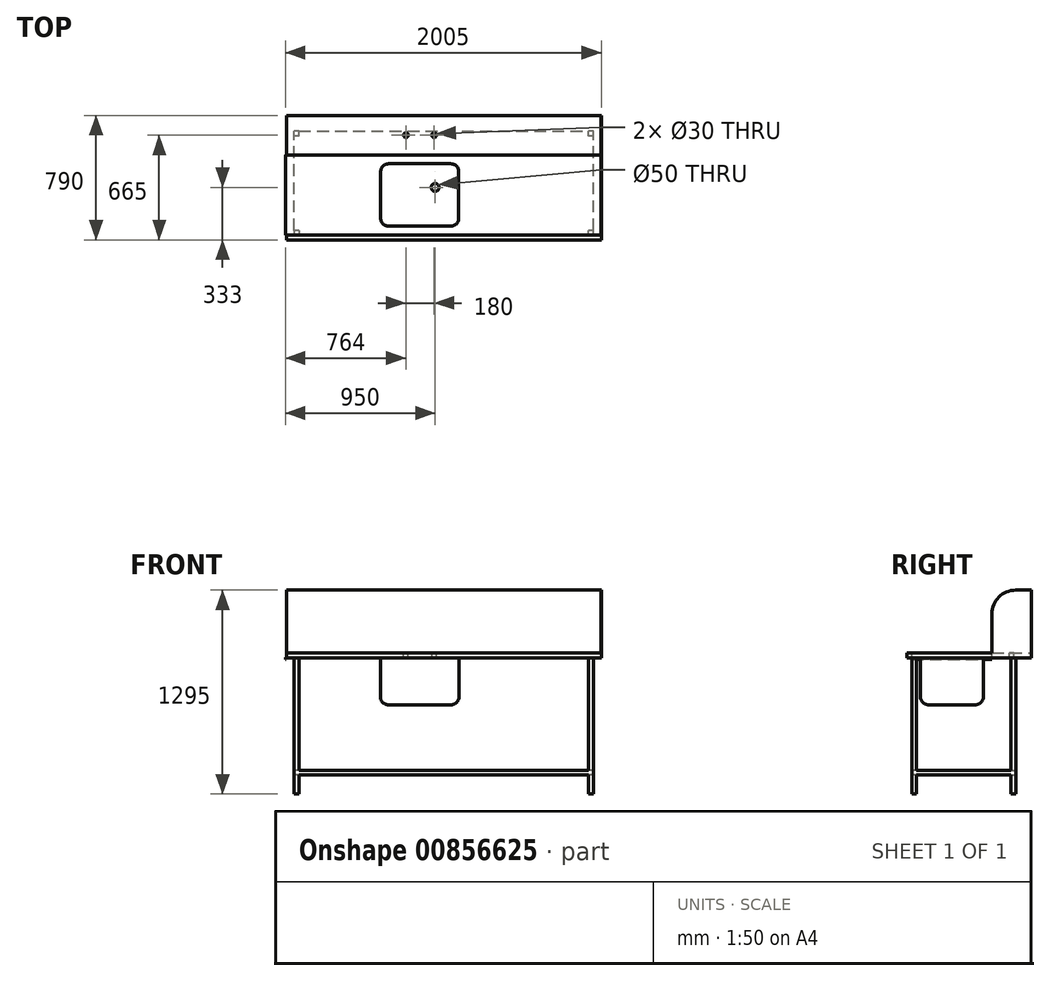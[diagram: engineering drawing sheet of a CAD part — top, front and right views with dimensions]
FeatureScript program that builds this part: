
annotation { "Feature Type Name" : "Feature", "Feature Type Description" : "" }
export const myFeature = defineFeature(function(context is Context, id is Id, definition is map)
    precondition{}
    {
        {
            var Q0;
            Q0=qCreatedBy(makeId("Top.planeOp"),FACE);
            var sketch = newSketch(context, id + "F0", { "sketchPlane" : qUnion([Q0])});
            skLineSegment(sketch, "E0.bottom", {"start": v(0, 0) * mm, "end": v(2000, 0) * mm});
            skLineSegment(sketch, "E0.top", {"start": v(0, 790) * mm, "end": v(2000, 790) * mm});
            skLineSegment(sketch, "E0.left", {"start": v(0, 0) * mm, "end": v(0, 790) * mm});
            skLineSegment(sketch, "E0.right", {"start": v(2000, 0) * mm, "end": v(2000, 790) * mm});
            skSolve(sketch);
        }
        {
            var Q0;
            Q0 = qSketchRegion(id + "F0", true);
            extrude(context, id + "F1", {"entities" : qUnion([Q0]), "depth" : 30 * mm, "offsetDistance" : 25 * mm});
        }
        {
            var Q0;
            Q0=makeQuery(id+"F1.opExtrude","CAP_FACE",FACE,{"disambiguationData":[OSD([sQuery(id+"F0.wireOp",EDGE,"E0.bottom"),sQuery(id+"F0.wireOp",EDGE,"E0.top"),sQuery(id+"F0.wireOp",EDGE,"E0.left"),sQuery(id+"F0.wireOp",EDGE,"E0.right")])],"isStart":false});
            var sketch = newSketch(context, id + "F2", { "sketchPlane" : qUnion([Q0])});
            skLineSegment(sketch, "E1.bottom", {"start": v(0, 30) * mm, "end": v(1998, 30) * mm});
            skLineSegment(sketch, "E1.top", {"start": v(0, 540) * mm, "end": v(1998, 540) * mm});
            skLineSegment(sketch, "E1.left", {"start": v(0, 30) * mm, "end": v(0, 540) * mm});
            skLineSegment(sketch, "E1.right", {"start": v(1998, 30) * mm, "end": v(1998, 540) * mm});
            skSolve(sketch);
        }
        {
            var Q0;
            Q0 = qSketchRegion(id + "F2", true);
            extrude(context, id + "F3", {"entities" : qUnion([Q0]), "operationType" : NewBodyOperationType.REMOVE, "oppositeDirection" : true, "depth" : 28 * mm, "offsetDistance" : 25 * mm});
        }
        {
            var Q0;
            Q0=makeQuery(id+"F1.opExtrude","SWEPT_FACE",FACE,{"disambiguationData":[OSD([sQuery(id+"F0.wireOp",EDGE,"E0.left")])]});
            var sketch = newSketch(context, id + "F4", { "sketchPlane" : qUnion([Q0])});
            skLineSegment(sketch, "E2.bottom", {"start": v(-540, 2) * mm, "end": v(-30, 2) * mm});
            skLineSegment(sketch, "E2.top", {"start": v(-540, 0) * mm, "end": v(-30, 0) * mm});
            skLineSegment(sketch, "E2.left", {"start": v(-540, 2) * mm, "end": v(-540, 0) * mm});
            skLineSegment(sketch, "E2.right", {"start": v(-30, 2) * mm, "end": v(-30, 0) * mm});
            skSolve(sketch);
        }
        {
            var Q0;
            Q0 = qSketchRegion(id + "F4", true);
            extrude(context, id + "F5", {"entities" : qUnion([Q0]), "operationType" : NewBodyOperationType.ADD, "depth" : 3 * mm, "offsetDistance" : 25 * mm});
        }
        {
            var Q0;
            Q0=makeQuery(id+"F5.opExtrude","CAP_FACE",FACE,{"disambiguationData":[OSD([sQuery(id+"F4.wireOp",EDGE,"E2.bottom"),sQuery(id+"F4.wireOp",EDGE,"E2.top"),sQuery(id+"F4.wireOp",EDGE,"E2.left"),sQuery(id+"F4.wireOp",EDGE,"E2.right")])],"isStart":false});
            var Q1;
            Q1=makeQuery(id+"F5.opExtrude","CAP_EDGE",EDGE,{"disambiguationData":[OSD([sQuery(id+"F4.wireOp",EDGE,"E2.top")])],"isStart":false});
            revolve(context, id + "F6", {"operationType" : NewBodyOperationType.ADD, "surfaceOperationType" : NewSurfaceOperationType.NEW, "entities" : qUnion([Q0]), "axis" : qUnion([Q1]), "revolveType" : RevolveType.ONE_DIRECTION, "oppositeDirection" : true, "angle" : 90 * degree});
        }
        {
            var Q0;
            {var subQ0=sQuery(id+"F4.wireOp",EDGE,"E2.top");Q0=makeQuery(id+"F6.boolean.opBoolean","MERGE",FACE,{"derivedFrom":[makeQuery(id+"F5.boolean.opBoolean","MERGE",FACE,{"derivedFrom":[makeQuery(id+"F1.opExtrude","CAP_FACE",FACE,{"disambiguationData":[OSD([sQuery(id+"F0.wireOp",EDGE,"E0.bottom"),sQuery(id+"F0.wireOp",EDGE,"E0.top"),sQuery(id+"F0.wireOp",EDGE,"E0.left"),sQuery(id+"F0.wireOp",EDGE,"E0.right")])],"isStart":true}),makeQuery(id+"F5.opExtrude","SWEPT_FACE",FACE,{"disambiguationData":[OSD([subQ0])]})]}),makeQuery(id+"F6.opRevolve","CAP_FACE",FACE,{"disambiguationData":[OSD([sQuery(id+"F4.wireOp",EDGE,"E2.bottom"),subQ0,sQuery(id+"F4.wireOp",EDGE,"E2.left"),sQuery(id+"F4.wireOp",EDGE,"E2.right")])],"isStart":false})]});}
            var sketch = newSketch(context, id + "F7", { "sketchPlane" : qUnion([Q0])});
            skLineSegment(sketch, "E3.bottom", {"start": v(-5, -540) * mm, "end": v(-3, -540) * mm});
            skLineSegment(sketch, "E3.top", {"start": v(-5, -30) * mm, "end": v(-3, -30) * mm});
            skLineSegment(sketch, "E3.left", {"start": v(-5, -540) * mm, "end": v(-5, -30) * mm});
            skLineSegment(sketch, "E3.right", {"start": v(-3, -540) * mm, "end": v(-3, -30) * mm});
            skSolve(sketch);
        }
        {
            var Q0;
            Q0 = qSketchRegion(id + "F7", true);
            extrude(context, id + "F8", {"entities" : qUnion([Q0]), "operationType" : NewBodyOperationType.ADD, "depth" : 10 * mm, "offsetDistance" : 25 * mm});
        }
        {
            var Q0;
            Q0=makeQuery(id+"F5.boolean.opBoolean","MERGE",FACE,{"derivedFrom":[makeQuery(id+"F3.boolean.opBoolean","COPY",FACE,{"derivedFrom":makeQuery(id+"F3.opExtrude","CAP_FACE",FACE,{"disambiguationData":[OSD([sQuery(id+"F2.wireOp",EDGE,"E1.bottom"),sQuery(id+"F2.wireOp",EDGE,"E1.top"),sQuery(id+"F2.wireOp",EDGE,"E1.left"),sQuery(id+"F2.wireOp",EDGE,"E1.right")])],"isStart":false})}),makeQuery(id+"F5.opExtrude","SWEPT_FACE",FACE,{"disambiguationData":[OSD([sQuery(id+"F4.wireOp",EDGE,"E2.bottom")])]})]});
            var sketch = newSketch(context, id + "F9", { "sketchPlane" : qUnion([Q0])});
            skLineSegment(sketch, "E4.bottom", {"start": v(1097, 485) * mm, "end": v(597, 485) * mm});
            skLineSegment(sketch, "E4.top", {"start": v(1097, 85) * mm, "end": v(597, 85) * mm});
            skLineSegment(sketch, "E4.left", {"start": v(1097, 485) * mm, "end": v(1097, 85) * mm});
            skLineSegment(sketch, "E4.right", {"start": v(597, 485) * mm, "end": v(597, 85) * mm});
            skPoint(sketch, "E4.middle", {"position": v(847, 285) * mm});
            skPoint(sketch, "E4.middle.positionSnap0", {"position": v(1998, 285) * mm});
            skPoint(sketch, "E4.middle.positionSnap1", {"position": v(847, 540) * mm});
            skPoint(sketch, "E4.centerSnap0", {"position": v(1998, 285) * mm});
            skPoint(sketch, "E4.centerSnap1", {"position": v(847, 540) * mm});
            skSolve(sketch);
        }
        {
            var Q0;
            Q0 = qSketchRegion(id + "F9", true);
            extrude(context, id + "F10", {"entities" : qUnion([Q0]), "operationType" : NewBodyOperationType.ADD, "oppositeDirection" : true, "depth" : 300 * mm, "offsetDistance" : 25 * mm});
        }
        {
            var Q0;
            Q0=makeQuery(id+"F5.boolean.opBoolean","MERGE",FACE,{"derivedFrom":[makeQuery(id+"F3.boolean.opBoolean","COPY",FACE,{"derivedFrom":makeQuery(id+"F3.opExtrude","CAP_FACE",FACE,{"disambiguationData":[OSD([sQuery(id+"F2.wireOp",EDGE,"E1.bottom"),sQuery(id+"F2.wireOp",EDGE,"E1.top"),sQuery(id+"F2.wireOp",EDGE,"E1.left"),sQuery(id+"F2.wireOp",EDGE,"E1.right")])],"isStart":false})}),makeQuery(id+"F5.opExtrude","SWEPT_FACE",FACE,{"disambiguationData":[OSD([sQuery(id+"F4.wireOp",EDGE,"E2.bottom")])]})]});
            var sketch = newSketch(context, id + "F11", { "sketchPlane" : qUnion([Q0])});
            skLineSegment(sketch, "E5.bottom", {"start": v(1095, 483) * mm, "end": v(599, 483) * mm});
            skLineSegment(sketch, "E5.top", {"start": v(1095, 87) * mm, "end": v(599, 87) * mm});
            skLineSegment(sketch, "E5.left", {"start": v(1095, 483) * mm, "end": v(1095, 87) * mm});
            skLineSegment(sketch, "E5.right", {"start": v(599, 483) * mm, "end": v(599, 87) * mm});
            skPoint(sketch, "E5.middle", {"position": v(847, 285) * mm});
            skPoint(sketch, "E5.middle.positionSnap0", {"position": v(1998, 285) * mm});
            skPoint(sketch, "E5.middle.positionSnap1", {"position": v(847, 540) * mm});
            skPoint(sketch, "E5.centerSnap0", {"position": v(1998, 285) * mm});
            skPoint(sketch, "E5.centerSnap1", {"position": v(847, 540) * mm});
            skSolve(sketch);
        }
        {
            var Q0;
            Q0 = qSketchRegion(id + "F11", true);
            extrude(context, id + "F12", {"entities" : qUnion([Q0]), "operationType" : NewBodyOperationType.REMOVE, "oppositeDirection" : true, "depth" : 298 * mm, "offsetDistance" : 25 * mm});
        }
        {
            var Q0;
            Q0=makeQuery(id+"F12.boolean.opBoolean","COPY",EDGE,{"derivedFrom":makeQuery(id+"F12.opExtrude","SWEPT_EDGE",EDGE,{"disambiguationData":[OSD([sQuery(id+"F11.wireOp",EDGE,"E5.bottom"),sQuery(id+"F11.wireOp",EDGE,"E5.right")])]})});
            var Q1;
            Q1=makeQuery(id+"F12.boolean.opBoolean","COPY",EDGE,{"derivedFrom":makeQuery(id+"F12.opExtrude","SWEPT_EDGE",EDGE,{"disambiguationData":[OSD([sQuery(id+"F11.wireOp",EDGE,"E5.bottom"),sQuery(id+"F11.wireOp",EDGE,"E5.left")])]})});
            var Q2;
            Q2=makeQuery(id+"F12.boolean.opBoolean","COPY",EDGE,{"derivedFrom":makeQuery(id+"F12.opExtrude","SWEPT_EDGE",EDGE,{"disambiguationData":[OSD([sQuery(id+"F11.wireOp",EDGE,"E5.top"),sQuery(id+"F11.wireOp",EDGE,"E5.left")])]})});
            var Q3;
            Q3=makeQuery(id+"F12.boolean.opBoolean","COPY",EDGE,{"derivedFrom":makeQuery(id+"F12.opExtrude","SWEPT_EDGE",EDGE,{"disambiguationData":[OSD([sQuery(id+"F11.wireOp",EDGE,"E5.top"),sQuery(id+"F11.wireOp",EDGE,"E5.right")])]})});
            var Q4;
            Q4=makeQuery(id+"F12.boolean.opBoolean","COPY",EDGE,{"derivedFrom":makeQuery(id+"F12.opExtrude","CAP_EDGE",EDGE,{"disambiguationData":[OSD([sQuery(id+"F11.wireOp",EDGE,"E5.right")])],"isStart":false})});
            var Q5;
            Q5=makeQuery(id+"F12.boolean.opBoolean","COPY",EDGE,{"derivedFrom":makeQuery(id+"F12.opExtrude","CAP_EDGE",EDGE,{"disambiguationData":[OSD([sQuery(id+"F11.wireOp",EDGE,"E5.top")])],"isStart":false})});
            var Q6;
            Q6=makeQuery(id+"F12.boolean.opBoolean","COPY",EDGE,{"derivedFrom":makeQuery(id+"F12.opExtrude","CAP_EDGE",EDGE,{"disambiguationData":[OSD([sQuery(id+"F11.wireOp",EDGE,"E5.left")])],"isStart":false})});
            var Q7;
            Q7=makeQuery(id+"F12.boolean.opBoolean","COPY",EDGE,{"derivedFrom":makeQuery(id+"F12.opExtrude","CAP_EDGE",EDGE,{"disambiguationData":[OSD([sQuery(id+"F11.wireOp",EDGE,"E5.bottom")])],"isStart":false})});
            var Q8;
            Q8=makeQuery(id+"F10.opExtrude","SWEPT_EDGE",EDGE,{"disambiguationData":[OSD([sQuery(id+"F9.wireOp",EDGE,"E4.top"),sQuery(id+"F9.wireOp",EDGE,"E4.right")])]});
            var Q9;
            Q9=makeQuery(id+"F10.opExtrude","SWEPT_EDGE",EDGE,{"disambiguationData":[OSD([sQuery(id+"F9.wireOp",EDGE,"E4.bottom"),sQuery(id+"F9.wireOp",EDGE,"E4.right")])]});
            var Q10;
            Q10=makeQuery(id+"F10.opExtrude","SWEPT_EDGE",EDGE,{"disambiguationData":[OSD([sQuery(id+"F9.wireOp",EDGE,"E4.top"),sQuery(id+"F9.wireOp",EDGE,"E4.left")])]});
            var Q11;
            Q11=makeQuery(id+"F10.opExtrude","SWEPT_EDGE",EDGE,{"disambiguationData":[OSD([sQuery(id+"F9.wireOp",EDGE,"E4.bottom"),sQuery(id+"F9.wireOp",EDGE,"E4.left")])]});
            var Q12;
            Q12=makeQuery(id+"F10.opExtrude","CAP_EDGE",EDGE,{"disambiguationData":[OSD([sQuery(id+"F9.wireOp",EDGE,"E4.left")])],"isStart":false});
            var Q13;
            Q13=makeQuery(id+"F10.opExtrude","CAP_EDGE",EDGE,{"disambiguationData":[OSD([sQuery(id+"F9.wireOp",EDGE,"E4.top")])],"isStart":false});
            var Q14;
            Q14=makeQuery(id+"F10.opExtrude","CAP_EDGE",EDGE,{"disambiguationData":[OSD([sQuery(id+"F9.wireOp",EDGE,"E4.right")])],"isStart":false});
            var Q15;
            Q15=makeQuery(id+"F10.opExtrude","CAP_EDGE",EDGE,{"disambiguationData":[OSD([sQuery(id+"F9.wireOp",EDGE,"E4.bottom")])],"isStart":false});
            fillet(context, id + "F13", {"entities" : qUnion([Q0, Q1, Q2, Q3, Q4, Q5, Q6, Q7, Q8, Q9, Q10, Q11, Q12, Q13, Q14, Q15]), "radius" : 50 * mm, "tangentPropagation" : true, "allowEdgeOverflow" : false});
        }
        {
            var Q0;
            Q0=makeQuery(id+"F12.boolean.opBoolean","COPY",FACE,{"derivedFrom":makeQuery(id+"F12.opExtrude","CAP_FACE",FACE,{"disambiguationData":[OSD([sQuery(id+"F11.wireOp",EDGE,"E5.bottom"),sQuery(id+"F11.wireOp",EDGE,"E5.top"),sQuery(id+"F11.wireOp",EDGE,"E5.left"),sQuery(id+"F11.wireOp",EDGE,"E5.right")])],"isStart":false})});
            var sketch = newSketch(context, id + "F14", { "sketchPlane" : qUnion([Q0])});
            skCircle(sketch, "E6", {"center": v(945, 333) * mm, "radius": 25 * mm});
            skSolve(sketch);
        }
        {
            var Q0;
            Q0 = qSketchRegion(id + "F14", true);
            extrude(context, id + "F15", {"entities" : qUnion([Q0]), "operationType" : NewBodyOperationType.REMOVE, "endBound" : BoundingType.UP_TO_NEXT, "oppositeDirection" : true, "depth" : 25 * mm, "offsetDistance" : 25 * mm});
        }
        {
            var Q0;
            Q0=makeQuery(id+"F1.opExtrude","CAP_FACE",FACE,{"disambiguationData":[OSD([sQuery(id+"F0.wireOp",EDGE,"E0.bottom"),sQuery(id+"F0.wireOp",EDGE,"E0.top"),sQuery(id+"F0.wireOp",EDGE,"E0.left"),sQuery(id+"F0.wireOp",EDGE,"E0.right")])],"isStart":false});
            var sketch = newSketch(context, id + "F16", { "sketchPlane" : qUnion([Q0])});
            skCircle(sketch, "E7", {"center": v(759, 665) * mm, "radius": 15 * mm});
            skPoint(sketch, "E7.centerSnap0", {"position": v(0, 665) * mm});
            skCircle(sketch, "E8", {"center": v(939, 665) * mm, "radius": 15 * mm});
            skSolve(sketch);
        }
        {
            var Q0;
            Q0 = qSketchRegion(id + "F16", true);
            extrude(context, id + "F17", {"entities" : qUnion([Q0]), "operationType" : NewBodyOperationType.REMOVE, "endBound" : BoundingType.UP_TO_NEXT, "oppositeDirection" : true, "depth" : 25 * mm, "offsetDistance" : 25 * mm});
        }
        {
            var Q0;
            {var subQ0=sQuery(id+"F4.wireOp",EDGE,"E2.top");Q0=makeQuery(id+"F6.boolean.opBoolean","MERGE",FACE,{"derivedFrom":[makeQuery(id+"F5.boolean.opBoolean","MERGE",FACE,{"derivedFrom":[makeQuery(id+"F1.opExtrude","CAP_FACE",FACE,{"disambiguationData":[OSD([sQuery(id+"F0.wireOp",EDGE,"E0.bottom"),sQuery(id+"F0.wireOp",EDGE,"E0.top"),sQuery(id+"F0.wireOp",EDGE,"E0.left"),sQuery(id+"F0.wireOp",EDGE,"E0.right")])],"isStart":true}),makeQuery(id+"F5.opExtrude","SWEPT_FACE",FACE,{"disambiguationData":[OSD([subQ0])]})]}),makeQuery(id+"F6.opRevolve","CAP_FACE",FACE,{"disambiguationData":[OSD([sQuery(id+"F4.wireOp",EDGE,"E2.bottom"),subQ0,sQuery(id+"F4.wireOp",EDGE,"E2.left"),sQuery(id+"F4.wireOp",EDGE,"E2.right")])],"isStart":false})]});}
            var sketch = newSketch(context, id + "F18", { "sketchPlane" : qUnion([Q0])});
            skLineSegment(sketch, "E9.bottom", {"start": v(80, -60) * mm, "end": v(50, -60) * mm});
            skLineSegment(sketch, "E9.top", {"start": v(80, -30) * mm, "end": v(50, -30) * mm});
            skLineSegment(sketch, "E9.left", {"start": v(80, -60) * mm, "end": v(80, -30) * mm});
            skLineSegment(sketch, "E9.right", {"start": v(50, -60) * mm, "end": v(50, -30) * mm});
            skPoint(sketch, "E9.middle", {"position": v(65, -45) * mm});
            skLineSegment(sketch, "E10.bottom", {"start": v(1950, -30) * mm, "end": v(1920, -30) * mm});
            skLineSegment(sketch, "E10.top", {"start": v(1950, -60) * mm, "end": v(1920, -60) * mm});
            skLineSegment(sketch, "E10.left", {"start": v(1950, -30) * mm, "end": v(1950, -60) * mm});
            skLineSegment(sketch, "E10.right", {"start": v(1920, -30) * mm, "end": v(1920, -60) * mm});
            skPoint(sketch, "E10.middle", {"position": v(1935, -45) * mm});
            skLineSegment(sketch, "E11.bottom", {"start": v(1950, -660) * mm, "end": v(1920, -660) * mm});
            skLineSegment(sketch, "E11.top", {"start": v(1950, -690) * mm, "end": v(1920, -690) * mm});
            skLineSegment(sketch, "E11.left", {"start": v(1950, -660) * mm, "end": v(1950, -690) * mm});
            skLineSegment(sketch, "E11.right", {"start": v(1920, -660) * mm, "end": v(1920, -690) * mm});
            skPoint(sketch, "E11.middle", {"position": v(1935, -675) * mm});
            skLineSegment(sketch, "E12.bottom", {"start": v(80, -660) * mm, "end": v(50, -660) * mm});
            skLineSegment(sketch, "E12.top", {"start": v(80, -690) * mm, "end": v(50, -690) * mm});
            skLineSegment(sketch, "E12.left", {"start": v(80, -660) * mm, "end": v(80, -690) * mm});
            skLineSegment(sketch, "E12.right", {"start": v(50, -660) * mm, "end": v(50, -690) * mm});
            skPoint(sketch, "E12.middle", {"position": v(65, -675) * mm});
            skSolve(sketch);
        }
        {
            var Q0;
            Q0 = qSketchRegion(id + "F18", true);
            extrude(context, id + "F19", {"entities" : qUnion([Q0]), "operationType" : NewBodyOperationType.ADD, "depth" : 865 * mm, "offsetDistance" : 25 * mm});
        }
        {
            var Q0;
            Q0=makeQuery(id+"F19.opExtrude","CAP_FACE",FACE,{"disambiguationData":[OSD([sQuery(id+"F18.wireOp",EDGE,"E9.bottom"),sQuery(id+"F18.wireOp",EDGE,"E9.top"),sQuery(id+"F18.wireOp",EDGE,"E9.left"),sQuery(id+"F18.wireOp",EDGE,"E9.right")])],"isStart":false});
            cPlane(context, id + "F20", {"entities" : qUnion([Q0]), "cplaneType" : CPlaneType.OFFSET, "offset" : 150 * mm, "oppositeDirection" : true, "width" : 150 * mm, "height" : 150 * mm});
        }
        {
            var Q0;
            Q0=qCreatedBy(id+"F20.planeOp",FACE);
            var sketch = newSketch(context, id + "F21", { "sketchPlane" : qUnion([Q0])});
            skLineSegment(sketch, "E13.bottom", {"start": v(50, -30) * mm, "end": v(1950, -30) * mm});
            skLineSegment(sketch, "E13.top", {"start": v(50, -690) * mm, "end": v(1950, -690) * mm});
            skLineSegment(sketch, "E13.left", {"start": v(50, -30) * mm, "end": v(50, -690) * mm});
            skLineSegment(sketch, "E13.right", {"start": v(1950, -30) * mm, "end": v(1950, -690) * mm});
            skSolve(sketch);
        }
        {
            var Q0;
            Q0 = qSketchRegion(id + "F21", true);
            extrude(context, id + "F22", {"entities" : qUnion([Q0]), "operationType" : NewBodyOperationType.ADD, "depth" : 30 * mm, "offsetDistance" : 25 * mm});
        }
        {
            var Q0;
            Q0=makeQuery(id+"F1.opExtrude","CAP_FACE",FACE,{"disambiguationData":[OSD([sQuery(id+"F0.wireOp",EDGE,"E0.bottom"),sQuery(id+"F0.wireOp",EDGE,"E0.top"),sQuery(id+"F0.wireOp",EDGE,"E0.left"),sQuery(id+"F0.wireOp",EDGE,"E0.right")])],"isStart":false});
            var sketch = newSketch(context, id + "F23", { "sketchPlane" : qUnion([Q0])});
            skLineSegment(sketch, "E14", {"start": v(0, 540) * mm, "end": v(0, 790) * mm});
            skLineSegment(sketch, "E15", {"start": v(0, 790) * mm, "end": v(2000, 790) * mm});
            skLineSegment(sketch, "E16", {"start": v(2000, 790) * mm, "end": v(2000, 540) * mm});
            skLineSegment(sketch, "E17", {"start": v(2000, 540) * mm, "end": v(1998, 540) * mm});
            skLineSegment(sketch, "E18", {"start": v(1998, 540) * mm, "end": v(1998, 788) * mm});
            skLineSegment(sketch, "E19", {"start": v(1998, 788) * mm, "end": v(2, 788) * mm});
            skLineSegment(sketch, "E20", {"start": v(2, 788) * mm, "end": v(2, 540) * mm});
            skLineSegment(sketch, "E21", {"start": v(2, 540) * mm, "end": v(0, 540) * mm});
            skSolve(sketch);
        }
        {
            var Q0;
            Q0 = qSketchRegion(id + "F23", true);
            extrude(context, id + "F24", {"entities" : qUnion([Q0]), "operationType" : NewBodyOperationType.ADD, "depth" : 400 * mm, "offsetDistance" : 25 * mm});
        }
        {
            var Q0;
            Q0=makeQuery(id+"F24.opExtrude","CAP_EDGE",EDGE,{"disambiguationData":[OSD([sQuery(id+"F23.wireOp",EDGE,"E21")])],"isStart":false});
            var Q1;
            Q1=makeQuery(id+"F24.opExtrude","CAP_EDGE",EDGE,{"disambiguationData":[OSD([sQuery(id+"F23.wireOp",EDGE,"E17")])],"isStart":false});
            fillet(context, id + "F25", {"entities" : qUnion([Q0, Q1]), "radius" : 150 * mm, "tangentPropagation" : true, "allowEdgeOverflow" : false});
        }
    });
